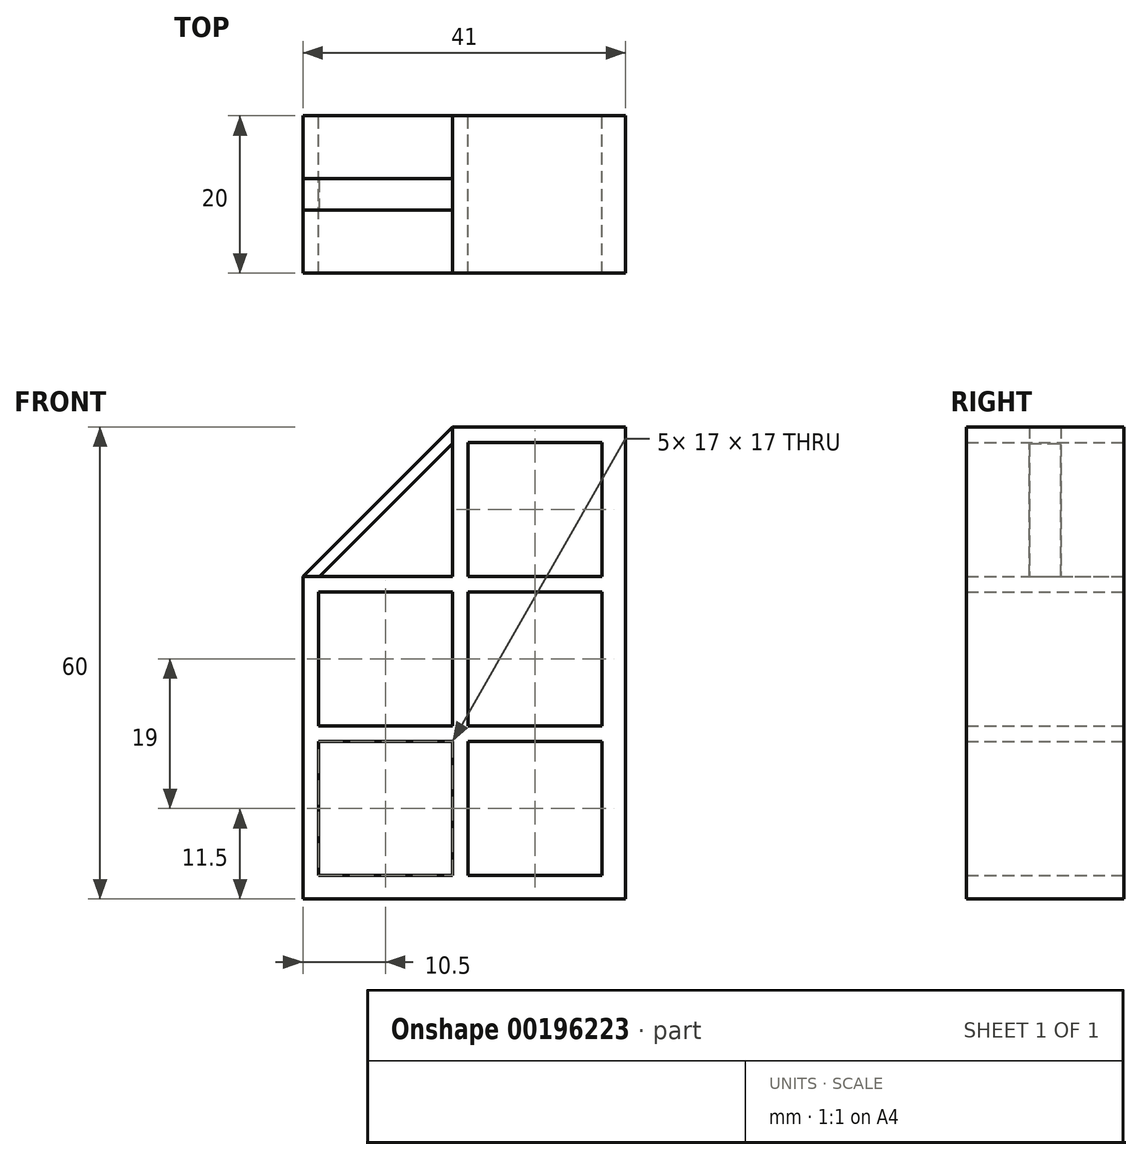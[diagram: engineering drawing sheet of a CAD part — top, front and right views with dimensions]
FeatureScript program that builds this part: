
annotation { "Feature Type Name" : "Feature", "Feature Type Description" : "" }
export const myFeature = defineFeature(function(context is Context, id is Id, definition is map)
    precondition{}
    {
        {
            var Q0;
            Q0=qCreatedBy(makeId("Front.planeOp"),FACE);
            var sketch = newSketch(context, id + "F0", { "sketchPlane" : qUnion([Q0])});
            skLineSegment(sketch, "E0.bottom", {"start": v(1, 3) * mm, "end": v(18, 3) * mm});
            skLineSegment(sketch, "E0.top", {"start": v(1, 20) * mm, "end": v(18, 20) * mm});
            skLineSegment(sketch, "E0.left", {"start": v(1, 3) * mm, "end": v(1, 20) * mm});
            skLineSegment(sketch, "E0.right", {"start": v(18, 3) * mm, "end": v(18, 20) * mm});
            skLineSegment(sketch, "E1.bottom", {"start": v(1, 22) * mm, "end": v(18, 22) * mm});
            skLineSegment(sketch, "E1.top", {"start": v(1, 39) * mm, "end": v(18, 39) * mm});
            skLineSegment(sketch, "E1.left", {"start": v(1, 22) * mm, "end": v(1, 39) * mm});
            skLineSegment(sketch, "E1.right", {"start": v(18, 22) * mm, "end": v(18, 39) * mm});
            skLineSegment(sketch, "E2.bottom", {"start": v(1, 41) * mm, "end": v(18, 41) * mm});
            skLineSegment(sketch, "E2.top", {"start": v(1, 58) * mm, "end": v(18, 58) * mm});
            skLineSegment(sketch, "E2.left", {"start": v(1, 41) * mm, "end": v(1, 58) * mm});
            skLineSegment(sketch, "E2.right", {"start": v(18, 41) * mm, "end": v(18, 58) * mm});
            skLineSegment(sketch, "E3", {"start": v(18, 20) * mm, "end": v(18, 22) * mm, "construction": true});
            skLineSegment(sketch, "E4", {"start": v(18, 39) * mm, "end": v(18, 41) * mm, "construction": true});
            skLineSegment(sketch, "E5.bottom", {"start": v(-1, 3) * mm, "end": v(-18, 3) * mm});
            skLineSegment(sketch, "E5.top", {"start": v(-1, 20) * mm, "end": v(-18, 20) * mm});
            skLineSegment(sketch, "E5.left", {"start": v(-1, 3) * mm, "end": v(-1, 20) * mm});
            skLineSegment(sketch, "E5.right", {"start": v(-18, 3) * mm, "end": v(-18, 20) * mm});
            skLineSegment(sketch, "E6", {"start": v(-1, 3) * mm, "end": v(1, 3) * mm, "construction": true});
            skPoint(sketch, "E7", {"position": v(0, 3) * mm});
            skLineSegment(sketch, "E8.bottom", {"start": v(-1, 22) * mm, "end": v(-18, 22) * mm});
            skLineSegment(sketch, "E8.top", {"start": v(-1, 39) * mm, "end": v(-18, 39) * mm});
            skLineSegment(sketch, "E8.left", {"start": v(-1, 22) * mm, "end": v(-1, 39) * mm});
            skLineSegment(sketch, "E8.right", {"start": v(-18, 22) * mm, "end": v(-18, 39) * mm});
            skLineSegment(sketch, "E9", {"start": v(-20, 0) * mm, "end": v(21, 0) * mm});
            skLineSegment(sketch, "E10", {"start": v(21, 0) * mm, "end": v(21, 60) * mm});
            skLineSegment(sketch, "E11", {"start": v(21, 60) * mm, "end": v(-1, 60) * mm});
            skLineSegment(sketch, "E12", {"start": v(-1, 60) * mm, "end": v(-1, 41) * mm});
            skLineSegment(sketch, "E13", {"start": v(-1, 41) * mm, "end": v(-20, 41) * mm});
            skLineSegment(sketch, "E14", {"start": v(-20, 41) * mm, "end": v(-20, 0) * mm});
            skSolve(sketch);
        }
        {
            var Q0;
            Q0=makeQuery(id+"F0.imprint","IMPRINT",FACE,{"disambiguationData":[TD([[makeQuery(id+"F0.imprint","IMPRINT",EDGE,{"derivedFrom":sQuery(id+"F0.wireOp",EDGE,"E0.bottom")}),-1.0]])]});
            extrude(context, id + "F1", {"entities" : qUnion([Q0]), "endBound" : BoundingType.SYMMETRIC, "depth" : (400 / 20) * mm});
        }
        {
            var Q0;
            Q0=qCreatedBy(makeId("Front.planeOp"),FACE);
            var sketch = newSketch(context, id + "F2", { "sketchPlane" : qUnion([Q0])});
            skLineSegment(sketch, "E15", {"start": v(-1, 60) * mm, "end": v(-20, 41) * mm});
            skLineSegment(sketch, "E16", {"start": v(-20, 41) * mm, "end": v(-17.88, 41) * mm});
            skLineSegment(sketch, "E17", {"start": v(-17.88, 41) * mm, "end": v(-1, 57.88) * mm});
            skLineSegment(sketch, "E18", {"start": v(-1, 60) * mm, "end": v(-1, 57.88) * mm});
            skSolve(sketch);
        }
        {
            var Q0;
            Q0=makeQuery(id+"F2.imprint","IMPRINT",FACE,{"disambiguationData":[TD([[makeQuery(id+"F2.imprint","IMPRINT",EDGE,{"derivedFrom":sQuery(id+"F2.wireOp",EDGE,"E15")}),1.0]])]});
            extrude(context, id + "F3", {"entities" : qUnion([Q0]), "operationType" : NewBodyOperationType.ADD, "endBound" : BoundingType.SYMMETRIC, "depth" : 4 * mm});
        }
    });
